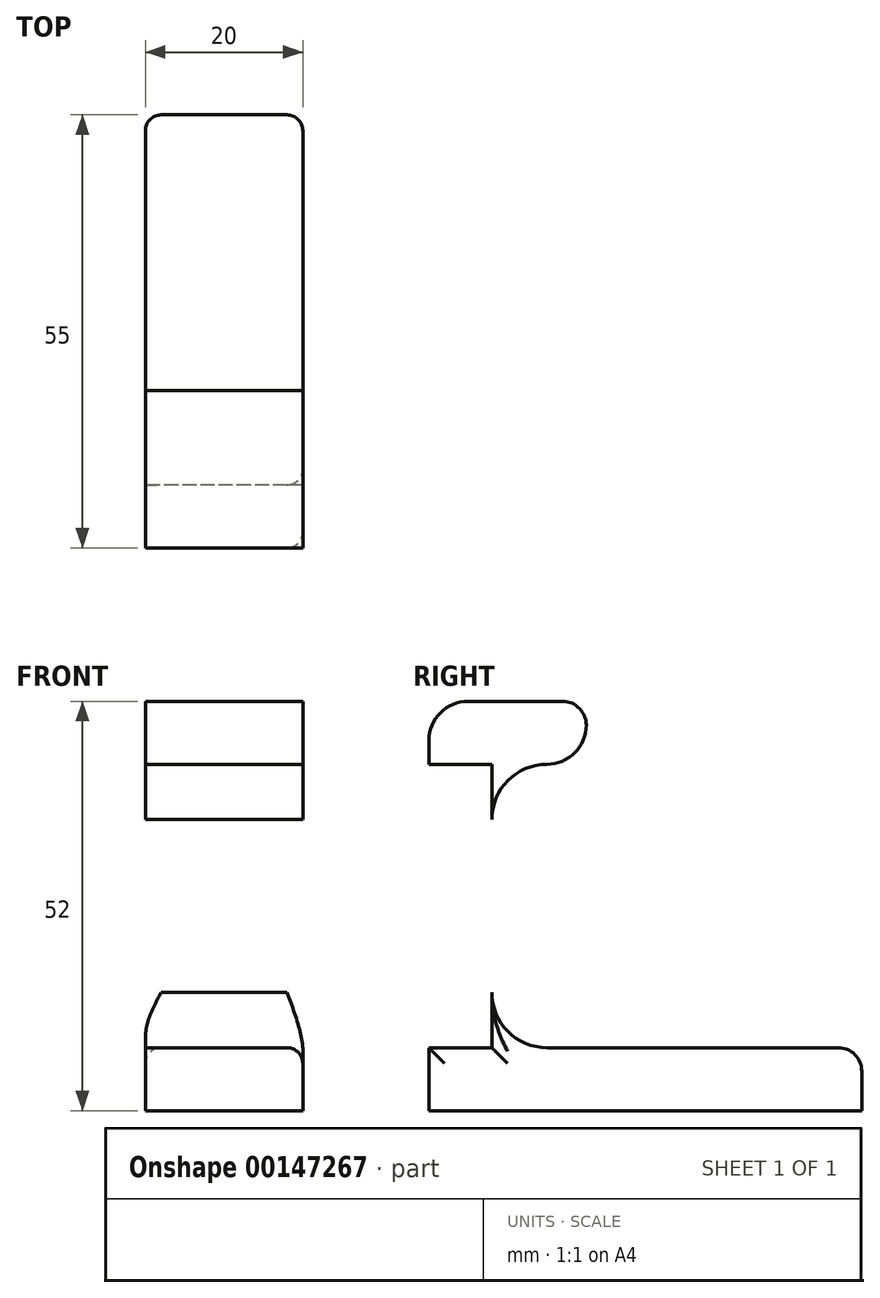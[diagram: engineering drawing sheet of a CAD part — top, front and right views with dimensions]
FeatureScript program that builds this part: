
annotation { "Feature Type Name" : "Feature", "Feature Type Description" : "" }
export const myFeature = defineFeature(function(context is Context, id is Id, definition is map)
    precondition{}
    {
        {
            var Q0;
            Q0=qCreatedBy(makeId("Right.planeOp"),FACE);
            var sketch = newSketch(context, id + "F0", { "sketchPlane" : qUnion([Q0])});
            skLineSegment(sketch, "E0.bottom", {"start": v(-30.3, 3.93) * mm, "end": v(21.7, 3.93) * mm});
            skLineSegment(sketch, "E0.top", {"start": v(-30.3, -4.07) * mm, "end": v(24.7, -4.07) * mm});
            skLineSegment(sketch, "E0.left", {"start": v(-30.3, 3.93) * mm, "end": v(-30.3, -4.07) * mm});
            skLineSegment(sketch, "E0.right", {"start": v(24.7, 0.93) * mm, "end": v(24.7, -4.07) * mm});
            skLineSegment(sketch, "E1.bottom", {"start": v(-30.3, 3.93) * mm, "end": v(-22.3, 3.93) * mm});
            skLineSegment(sketch, "E1.top", {"start": v(-30.3, 39.93) * mm, "end": v(-22.3, 39.93) * mm});
            skLineSegment(sketch, "E1.left", {"start": v(-30.3, 3.93) * mm, "end": v(-30.3, 39.93) * mm});
            skLineSegment(sketch, "E1.right", {"start": v(-22.3, 3.93) * mm, "end": v(-22.3, 39.93) * mm});
            skLineSegment(sketch, "E2.bottom", {"start": v(-30.3, 39.93) * mm, "end": v(-15.3, 39.93) * mm});
            skLineSegment(sketch, "E2.top", {"start": v(-25.3, 47.93) * mm, "end": v(-13.3, 47.93) * mm});
            skLineSegment(sketch, "E2.left", {"start": v(-30.3, 39.93) * mm, "end": v(-30.3, 42.93) * mm});
            skLineSegment(sketch, "E2.right", {"start": v(-10.3, 44.93) * mm, "end": v(-10.3, 44.93) * mm});
            skArc(sketch, "E3", {"start": v(-15.3, 39.93) * mm, "mid": v(-20.26, 37.87) * mm, "end": v(-22.3, 32.93) * mm});
            skArc(sketch, "E4", {"start": v(-22.3, 10.93) * mm, "mid": v(-20.26, 5.98) * mm, "end": v(-15.3, 3.93) * mm});
            skPoint(sketch, "E5.visualSharp", {"position": v(-10.3, 47.93) * mm});
            skArc(sketch, "E5.filletArc", {"start": v(-10.3, 44.93) * mm, "mid": v(-11.19, 47.05) * mm, "end": v(-13.3, 47.93) * mm});
            skPoint(sketch, "E6.visualSharp", {"position": v(-10.3, 39.93) * mm});
            skArc(sketch, "E6.filletArc", {"start": v(-15.3, 39.93) * mm, "mid": v(-11.77, 41.39) * mm, "end": v(-10.3, 44.93) * mm});
            skPoint(sketch, "E7.visualSharp", {"position": v(-30.3, 47.93) * mm});
            skArc(sketch, "E7.filletArc", {"start": v(-25.3, 47.93) * mm, "mid": v(-28.84, 46.46) * mm, "end": v(-30.3, 42.93) * mm});
            skPoint(sketch, "E8.visualSharp", {"position": v(24.7, 3.93) * mm});
            skArc(sketch, "E8.filletArc", {"start": v(24.7, 0.93) * mm, "mid": v(23.81, 3.05) * mm, "end": v(21.7, 3.93) * mm});
            skSolve(sketch);
        }
        {
            var Q0;
            Q0=makeQuery(id+"F0.imprint","IMPRINT",FACE,{"disambiguationData":[TD([[makeQuery(id+"F0.imprint","IMPRINT",EDGE,{"derivedFrom":sQuery(id+"F0.wireOp",EDGE,"E2.top")}),-1.0]])]});
            var Q1;
            {var subQ3=sQuery(id+"F0.wireOp",EDGE,"E1.bottom");Q1=makeQuery(id+"F0.imprint","IMPRINT",FACE,{"disambiguationData":[TD([[makeQuery(id+"F0.imprint","IMPRINT",EDGE,{"derivedFrom":subQ3}),1.0]])]});}
            var Q2;
            {var subQ3=sQuery(id+"F0.wireOp",EDGE,"E4");Q2=makeQuery(id+"F0.imprint","IMPRINT",FACE,{"disambiguationData":[TD([[makeQuery(id+"F0.imprint","IMPRINT",EDGE,{"derivedFrom":subQ3}),-1.0]])]});}
            var Q3;
            Q3=makeQuery(id+"F0.imprint","IMPRINT",FACE,{"disambiguationData":[TD([[makeQuery(id+"F0.imprint","IMPRINT",EDGE,{"derivedFrom":sQuery(id+"F0.wireOp",EDGE,"E0.top")}),1.0]])]});
            var Q4;
            {var subQ3=sQuery(id+"F0.wireOp",EDGE,"E3");Q4=makeQuery(id+"F0.imprint","IMPRINT",FACE,{"disambiguationData":[TD([[makeQuery(id+"F0.imprint","IMPRINT",EDGE,{"derivedFrom":subQ3}),-1.0]])]});}
            extrude(context, id + "F1", {"entities" : qUnion([Q0, Q1, Q2, Q3, Q4]), "depth" : 20 * mm});
        }
        {
            var Q0;
            Q0=makeQuery(id+"F1.opExtrude","CAP_EDGE",EDGE,{"disambiguationData":[OSD([sQuery(id+"F0.wireOp",EDGE,"E0.bottom")])],"isStart":false});
            var Q1;
            Q1=makeQuery(id+"F1.opExtrude","CAP_EDGE",EDGE,{"disambiguationData":[OSD([sQuery(id+"F0.wireOp",EDGE,"E4")])],"isStart":false});
            var Q2;
            Q2=makeQuery(id+"F1.opExtrude","CAP_EDGE",EDGE,{"disambiguationData":[OSD([sQuery(id+"F0.wireOp",EDGE,"E1.right")])],"isStart":false});
            var Q3;
            Q3=makeQuery(id+"F1.opExtrude","CAP_EDGE",EDGE,{"disambiguationData":[OSD([sQuery(id+"F0.wireOp",EDGE,"E3")])],"isStart":false});
            var Q4;
            Q4=makeQuery(id+"F1.opExtrude","CAP_EDGE",EDGE,{"disambiguationData":[OSD([sQuery(id+"F0.wireOp",EDGE,"E6.filletArc")])],"isStart":false});
            var Q5;
            Q5=makeQuery(id+"F1.opExtrude","CAP_EDGE",EDGE,{"disambiguationData":[OSD([sQuery(id+"F0.wireOp",EDGE,"E8.filletArc")])],"isStart":false});
            var Q6;
            Q6=makeQuery(id+"F1.opExtrude","CAP_EDGE",EDGE,{"disambiguationData":[OSD([sQuery(id+"F0.wireOp",EDGE,"E5.filletArc")])],"isStart":false});
            var Q7;
            Q7=makeQuery(id+"F1.opExtrude","CAP_EDGE",EDGE,{"disambiguationData":[OSD([sQuery(id+"F0.wireOp",EDGE,"E2.top")])],"isStart":false});
            var Q8;
            Q8=makeQuery(id+"F1.opExtrude","CAP_EDGE",EDGE,{"disambiguationData":[OSD([sQuery(id+"F0.wireOp",EDGE,"E7.filletArc")])],"isStart":false});
            var Q9;
            Q9=makeQuery(id+"F1.opExtrude","CAP_EDGE",EDGE,{"disambiguationData":[OSD([sQuery(id+"F0.wireOp",EDGE,"E0.right")])],"isStart":false});
            var Q10;
            Q10=makeQuery(id+"F1.opExtrude","CAP_EDGE",EDGE,{"disambiguationData":[OSD([sQuery(id+"F0.wireOp",EDGE,"E0.left"),sQuery(id+"F0.wireOp",EDGE,"E1.left"),sQuery(id+"F0.wireOp",EDGE,"E2.left")])],"isStart":false});
            var Q11;
            Q11=makeQuery(id+"F1.opExtrude","CAP_EDGE",EDGE,{"disambiguationData":[OSD([sQuery(id+"F0.wireOp",EDGE,"E0.right")])],"isStart":true});
            var Q12;
            Q12=makeQuery(id+"F1.opExtrude","CAP_EDGE",EDGE,{"disambiguationData":[OSD([sQuery(id+"F0.wireOp",EDGE,"E8.filletArc")])],"isStart":true});
            fillet(context, id + "F2", {"entities" : qUnion([Q0, Q1, Q2, Q3, Q4, Q5, Q6, Q7, Q8, Q9, Q10, Q11, Q12]), "radius" : 2 * mm, "tangentPropagation" : true, "allowEdgeOverflow" : false});
        }
    });
